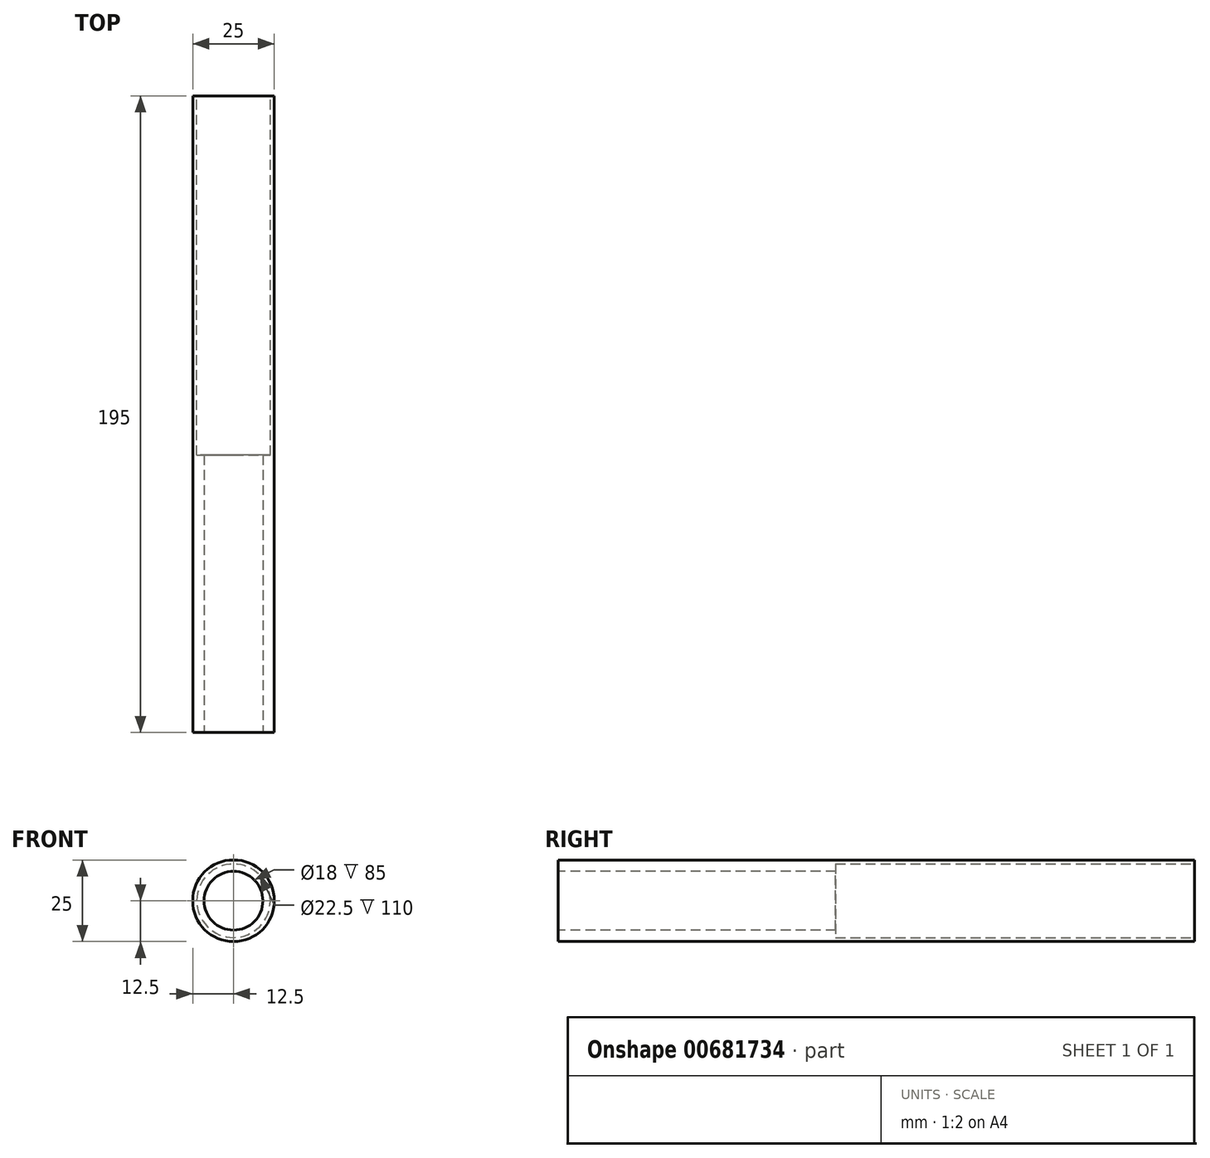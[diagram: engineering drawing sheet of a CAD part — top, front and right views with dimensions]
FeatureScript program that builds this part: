
annotation { "Feature Type Name" : "Feature", "Feature Type Description" : "" }
export const myFeature = defineFeature(function(context is Context, id is Id, definition is map)
    precondition{}
    {
        {
            var Q0;
            Q0=qCreatedBy(makeId("Front.planeOp"),FACE);
            var sketch = newSketch(context, id + "F0", { "sketchPlane" : qUnion([Q0])});
            skCircle(sketch, "E0", {"center": v(0, 0) * mm, "radius": 12.5 * mm});
            skCircle(sketch, "E1", {"center": v(0, 0) * mm, "radius": 9 * mm});
            skSolve(sketch);
        }
        {
            var Q0;
            Q0=makeQuery(id+"F0.imprint","IMPRINT",FACE,{"disambiguationData":[TD([[makeQuery(id+"F0.imprint","IMPRINT",EDGE,{"derivedFrom":sQuery(id+"F0.wireOp",EDGE,"E0")}),1.0]])]});
            extrude(context, id + "F1", {"entities" : qUnion([Q0]), "oppositeDirection" : true, "depth" : 195 * mm, "offsetDistance" : 25 * mm});
        }
        {
            var Q0;
            Q0=makeQuery(id+"F1.opExtrude","CAP_FACE",FACE,{"disambiguationData":[OSD([sQuery(id+"F0.wireOp",EDGE,"E0"),sQuery(id+"F0.wireOp",EDGE,"E1")])],"isStart":false});
            var sketch = newSketch(context, id + "F2", { "sketchPlane" : qUnion([Q0])});
            skCircle(sketch, "E2", {"center": v(0, 0) * mm, "radius": 11.25 * mm});
            skSolve(sketch);
        }
        {
            var Q0;
            Q0=makeQuery(id+"F2.imprint","IMPRINT",FACE,{"disambiguationData":[TD([[makeQuery(id+"F2.imprint","IMPRINT",EDGE,{"derivedFrom":sQuery(id+"F2.wireOp",EDGE,"E2")}),1.0]])]});
            extrude(context, id + "F3", {"entities" : qUnion([Q0]), "operationType" : NewBodyOperationType.REMOVE, "oppositeDirection" : true, "depth" : 110 * mm, "offsetDistance" : 25 * mm});
        }
    });
